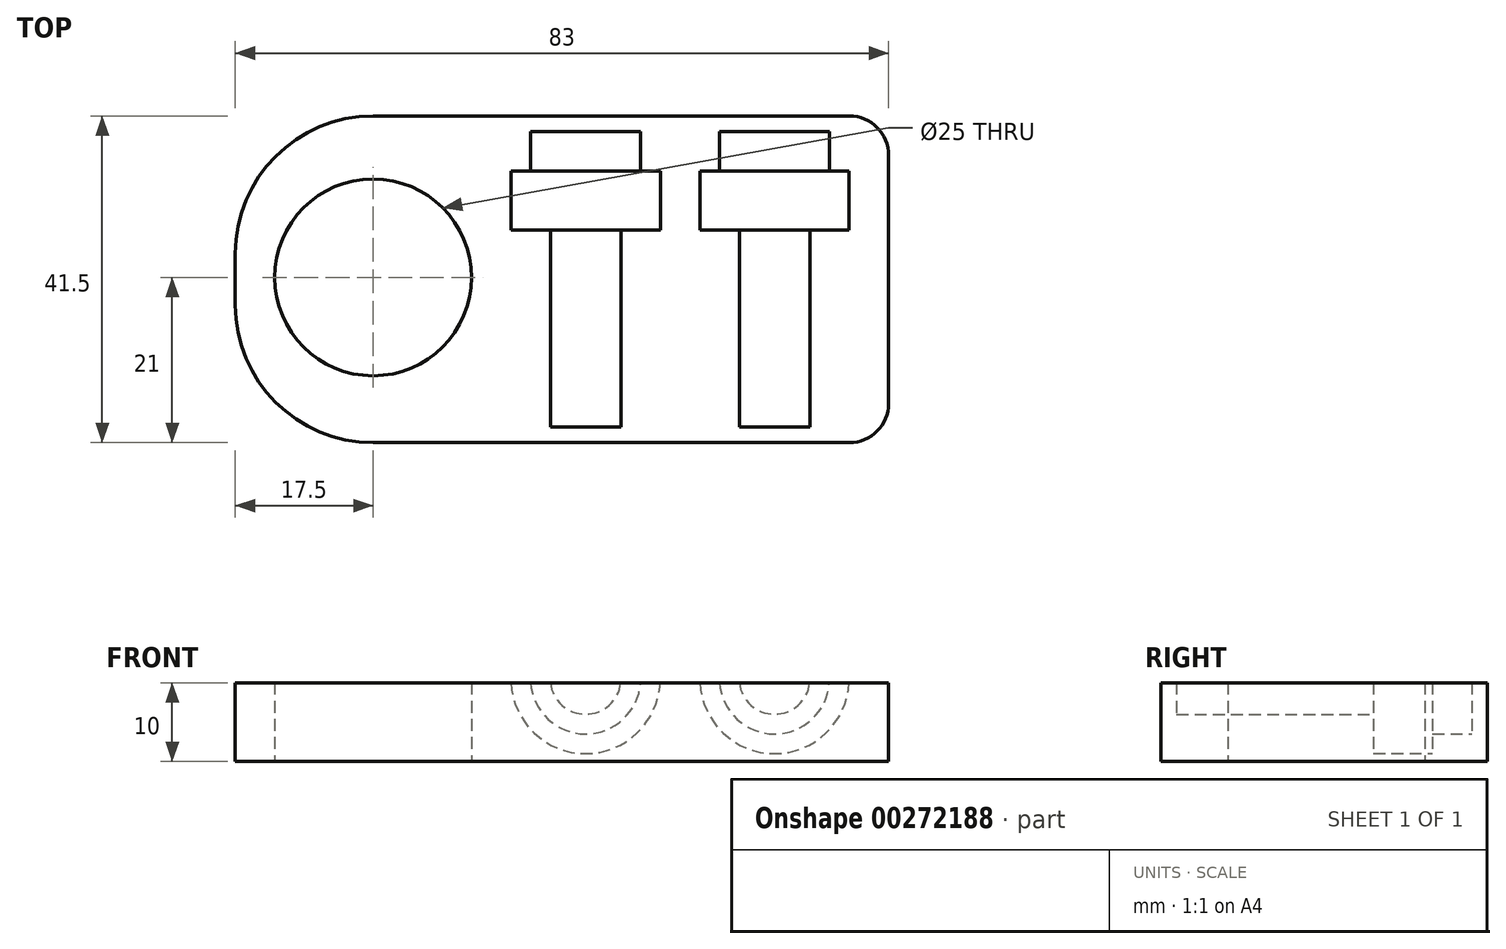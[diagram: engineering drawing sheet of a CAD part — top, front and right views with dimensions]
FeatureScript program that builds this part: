
annotation { "Feature Type Name" : "Feature", "Feature Type Description" : "" }
export const myFeature = defineFeature(function(context is Context, id is Id, definition is map)
    precondition{}
    {
        {
            var Q0;
            Q0=qCreatedBy(makeId("Top.planeOp"),FACE);
            var sketch = newSketch(context, id + "F0", { "sketchPlane" : qUnion([Q0])});
            skLineSegment(sketch, "E0.bottom", {"start": v(17.5, 0) * mm, "end": v(78, 0) * mm});
            skLineSegment(sketch, "E0.top", {"start": v(17.5, 41.5) * mm, "end": v(78, 41.5) * mm});
            skLineSegment(sketch, "E0.left", {"start": v(0, 17.5) * mm, "end": v(0, 24) * mm});
            skLineSegment(sketch, "E0.right", {"start": v(83, 5) * mm, "end": v(83, 36.5) * mm});
            skLineSegment(sketch, "E1.bottom", {"start": v(0, 0) * mm, "end": v(17.5, 0) * mm, "construction": true});
            skLineSegment(sketch, "E1.top", {"start": v(0, 21) * mm, "end": v(17.5, 21) * mm, "construction": true});
            skLineSegment(sketch, "E1.left", {"start": v(0, 0) * mm, "end": v(0, 21) * mm, "construction": true});
            skLineSegment(sketch, "E1.right", {"start": v(17.5, 0) * mm, "end": v(17.5, 21) * mm, "construction": true});
            skCircle(sketch, "E2", {"center": v(17.5, 21) * mm, "radius": 12.5 * mm});
            skPoint(sketch, "E3.visualSharp", {"position": v(0, 0) * mm});
            skArc(sketch, "E3.filletArc", {"start": v(0, 17.5) * mm, "mid": v(5.13, 5.13) * mm, "end": v(17.5, 0) * mm});
            skPoint(sketch, "E4.visualSharp", {"position": v(0, 41.5) * mm});
            skArc(sketch, "E4.filletArc", {"start": v(17.5, 41.5) * mm, "mid": v(5.13, 36.37) * mm, "end": v(0, 24) * mm});
            skPoint(sketch, "E5.visualSharp", {"position": v(83, 41.5) * mm});
            skArc(sketch, "E5.filletArc", {"start": v(83, 36.5) * mm, "mid": v(81.54, 40.04) * mm, "end": v(78, 41.5) * mm});
            skPoint(sketch, "E6.visualSharp", {"position": v(83, 0) * mm});
            skArc(sketch, "E6.filletArc", {"start": v(78, 0) * mm, "mid": v(81.54, 1.46) * mm, "end": v(83, 5) * mm});
            skSolve(sketch);
        }
        {
            var Q0;
            Q0=makeQuery(id+"F0.imprint","IMPRINT",FACE,{"disambiguationData":[TD([[makeQuery(id+"F0.imprint","IMPRINT",EDGE,{"derivedFrom":sQuery(id+"F0.wireOp",EDGE,"E0.bottom")}),1.0]])]});
            extrude(context, id + "F1", {"entities" : qUnion([Q0]), "depth" : 10 * mm});
        }
        {
            var Q0;
            Q0=makeQuery(id+"F1.opExtrude","CAP_FACE",FACE,{"disambiguationData":[OSD([sQuery(id+"F0.wireOp",EDGE,"E0.bottom"),sQuery(id+"F0.wireOp",EDGE,"E0.top"),sQuery(id+"F0.wireOp",EDGE,"E0.right"),sQuery(id+"F0.wireOp",EDGE,"E2"),sQuery(id+"F0.wireOp",EDGE,"E3.filletArc"),sQuery(id+"F0.wireOp",EDGE,"E4.filletArc"),sQuery(id+"F0.wireOp",EDGE,"E5.filletArc"),sQuery(id+"F0.wireOp",EDGE,"E6.filletArc")])],"isStart":false});
            cPlane(context, id + "F2", {"entities" : qUnion([Q0]), "cplaneType" : CPlaneType.OFFSET, "offset" : .5 * mm, "width" : 150 * mm, "height" : 150 * mm});
        }
        {
            var Q0;
            Q0=qCreatedBy(id+"F2.planeOp",FACE);
            var sketch = newSketch(context, id + "F3", { "sketchPlane" : qUnion([Q0])});
            skLineSegment(sketch, "E7.bottom", {"start": v(0, 0) * mm, "end": v(44.5, 0) * mm, "construction": true});
            skLineSegment(sketch, "E7.top", {"start": v(0, 2) * mm, "end": v(44.5, 2) * mm, "construction": true});
            skLineSegment(sketch, "E7.left", {"start": v(0, 0) * mm, "end": v(0, 2) * mm, "construction": true});
            skLineSegment(sketch, "E7.right", {"start": v(44.5, 0) * mm, "end": v(44.5, 2) * mm, "construction": true});
            skLineSegment(sketch, "E8", {"start": v(44.5, 2) * mm, "end": v(68.5, 2) * mm, "construction": true});
            skLineSegment(sketch, "E9.bottom", {"start": v(44.5, 2) * mm, "end": v(49, 2) * mm});
            skLineSegment(sketch, "E9.left", {"start": v(44.5, 2) * mm, "end": v(44.5, 27) * mm});
            skLineSegment(sketch, "E9.right", {"start": v(49, 2) * mm, "end": v(49, 27) * mm});
            skLineSegment(sketch, "E10.bottom", {"start": v(49, 27) * mm, "end": v(54, 27) * mm});
            skLineSegment(sketch, "E10.top", {"start": v(51.5, 34.5) * mm, "end": v(54, 34.5) * mm});
            skLineSegment(sketch, "E10.left", {"start": v(44.5, 27) * mm, "end": v(44.5, 34.5) * mm});
            skLineSegment(sketch, "E10.right", {"start": v(54, 27) * mm, "end": v(54, 34.5) * mm});
            skLineSegment(sketch, "E11.top", {"start": v(44.5, 39.5) * mm, "end": v(51.5, 39.5) * mm});
            skLineSegment(sketch, "E11.left", {"start": v(44.5, 34.5) * mm, "end": v(44.5, 39.5) * mm});
            skLineSegment(sketch, "E11.right", {"start": v(51.5, 34.5) * mm, "end": v(51.5, 39.5) * mm});
            skLineSegment(sketch, "E12.bottom", {"start": v(68.5, 2) * mm, "end": v(73, 2) * mm});
            skLineSegment(sketch, "E12.left", {"start": v(68.5, 2) * mm, "end": v(68.5, 27) * mm});
            skLineSegment(sketch, "E12.right", {"start": v(73, 2) * mm, "end": v(73, 27) * mm});
            skLineSegment(sketch, "E13.bottom", {"start": v(73, 27) * mm, "end": v(78, 27) * mm});
            skLineSegment(sketch, "E13.top", {"start": v(75.5, 34.5) * mm, "end": v(78, 34.5) * mm});
            skLineSegment(sketch, "E13.left", {"start": v(68.5, 27) * mm, "end": v(68.5, 34.5) * mm});
            skLineSegment(sketch, "E13.right", {"start": v(78, 27) * mm, "end": v(78, 34.5) * mm});
            skLineSegment(sketch, "E14.top", {"start": v(68.5, 39.5) * mm, "end": v(75.5, 39.5) * mm});
            skLineSegment(sketch, "E14.left", {"start": v(68.5, 34.5) * mm, "end": v(68.5, 39.5) * mm});
            skLineSegment(sketch, "E14.right", {"start": v(75.5, 34.5) * mm, "end": v(75.5, 39.5) * mm});
            skSolve(sketch);
        }
        {
            var Q0;
            Q0=makeQuery(id+"F3.imprint","IMPRINT",FACE,{"disambiguationData":[TD([[makeQuery(id+"F3.imprint","IMPRINT",EDGE,{"derivedFrom":sQuery(id+"F3.wireOp",EDGE,"E9.bottom")}),1.0]])]});
            var Q1;
            Q1=sQuery(id+"F3.wireOp",EDGE,"E9.left");
            revolve(context, id + "F4", {"operationType" : NewBodyOperationType.REMOVE, "entities" : qUnion([Q0]), "axis" : qUnion([Q1]), "revolveType" : RevolveType.FULL, "oppositeDirection" : true});
        }
        {
            var Q0;
            Q0=makeQuery(id+"F3.imprint","IMPRINT",FACE,{"disambiguationData":[TD([[makeQuery(id+"F3.imprint","IMPRINT",EDGE,{"derivedFrom":sQuery(id+"F3.wireOp",EDGE,"E12.bottom")}),1.0]])]});
            var Q1;
            Q1=sQuery(id+"F3.wireOp",EDGE,"E12.left");
            revolve(context, id + "F5", {"operationType" : NewBodyOperationType.REMOVE, "entities" : qUnion([Q0]), "axis" : qUnion([Q1]), "revolveType" : RevolveType.FULL, "oppositeDirection" : true});
        }
    });
